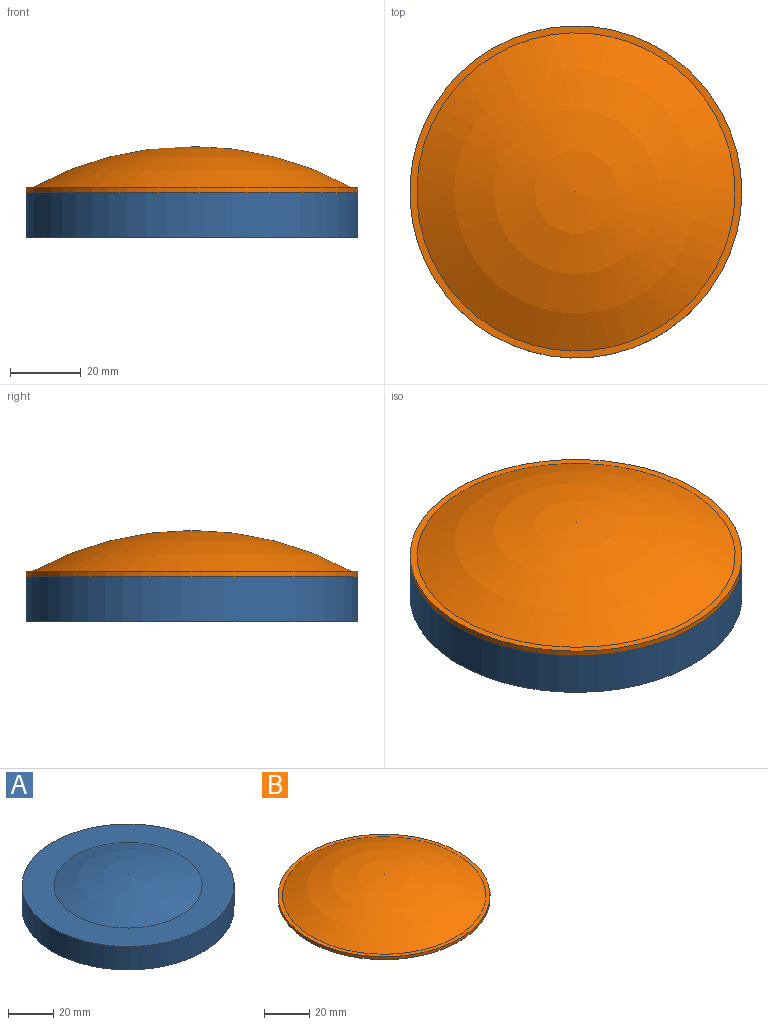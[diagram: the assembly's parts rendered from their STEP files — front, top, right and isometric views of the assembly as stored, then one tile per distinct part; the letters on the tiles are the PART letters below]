
ASSEMBLY  parts=2 mates=1
PART A: 4 faces, bbox 94x94x18.8 mm
  f0: plane 93.98x93.98mm, normal (0,0,-1), area 6936.8mm2, adj f1
  f1: cylinder r=46.99mm len=93.98mm, axis (0,0,1), area 3749.6mm2, adj f0,f2
  f2: plane 93.98x93.98mm, normal (0,0,1), area 3551.2mm2, adj f1,f3
  f3: sphere r=91.44mm, area 3502.4mm2, adj f2
PART B: 5 faces, bbox 94x94x13.1 mm
  f0: sphere r=93.98mm, area 6786.3mm2, adj f4
  f1: sphere r=93.98mm, area 4476.6mm2, adj f2
  f2: plane 93.98x93.98mm, normal (0,0,-1), area 2640.8mm2, adj f1,f3
  f3: cylinder r=46.99mm len=93.98mm, axis (0,0,1), area 465mm2, adj f2,f4
  f4: plane 93.98x93.98mm, normal (0,0,1), area 565.4mm2, adj f0,f3
PLACE A t=(-13.09,21.33,24.09)mm
PLACE B t=(-13.09,21.33,36.79)mm
MATE fastened A.f1 <-> B.f3  axis (0,0,1) through (-13.09,21.33,36.79)mm
